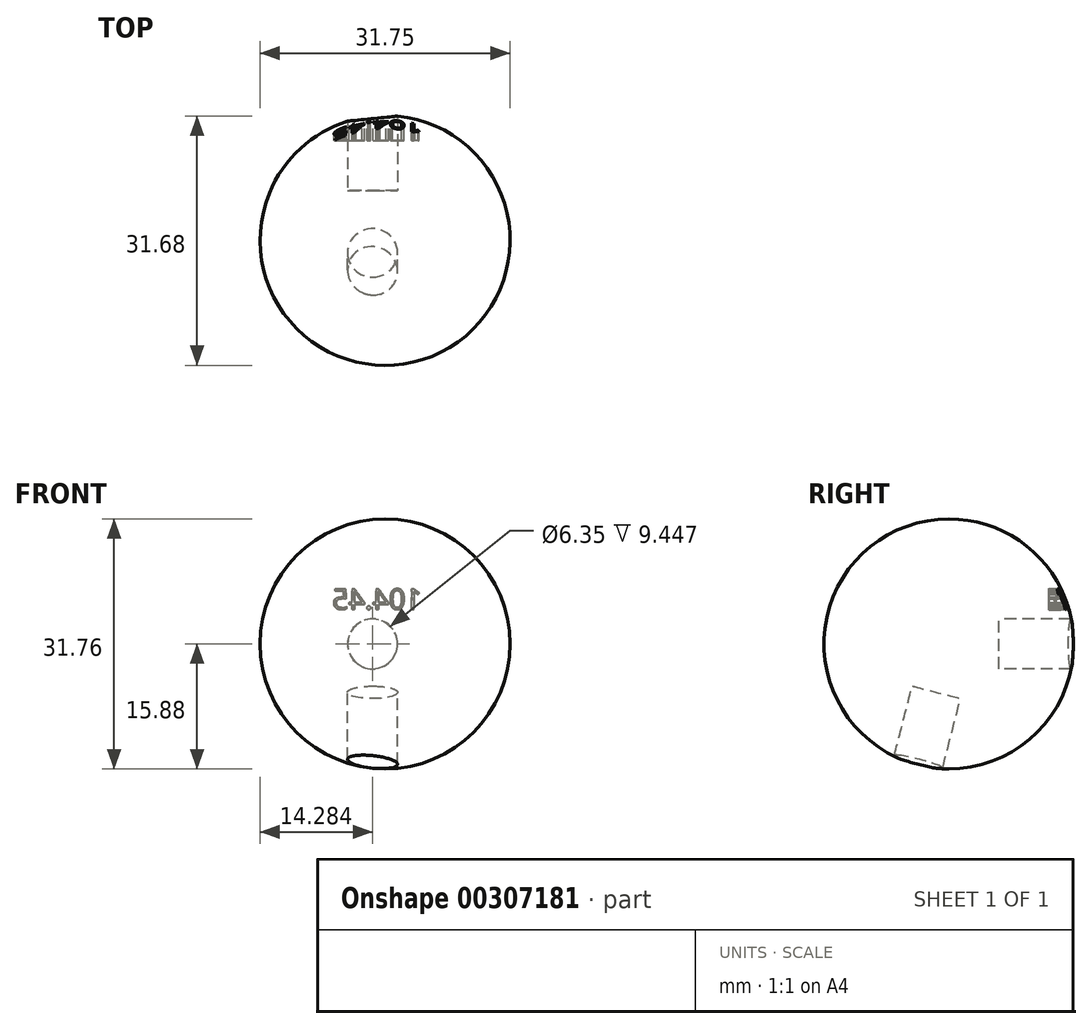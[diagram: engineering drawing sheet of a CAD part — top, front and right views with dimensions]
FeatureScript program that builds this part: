
annotation { "Feature Type Name" : "Feature", "Feature Type Description" : "" }
export const myFeature = defineFeature(function(context is Context, id is Id, definition is map)
    precondition{}
    {
        {
            var Q0;
            Q0=qCreatedBy(makeId("Top.planeOp"),FACE);
            var sketch = newSketch(context, id + "F0", { "sketchPlane" : qUnion([Q0])});
            skCircle(sketch, "E0", {"center": v(0, 0) * mm, "radius": 15.88 * mm});
            skSolve(sketch);
        }
        {
            var Q0;
            Q0=qCreatedBy(makeId("Front.planeOp"),FACE);
            var sketch = newSketch(context, id + "F1", { "sketchPlane" : qUnion([Q0])});
            skArc(sketch, "E1", {"start": v(0, 15.88) * mm, "mid": v(-15.88, 0) * mm, "end": v(0, -15.88) * mm});
            skLineSegment(sketch, "E2", {"start": v(0, -15.88) * mm, "end": v(0, 15.88) * mm});
            skSolve(sketch);
        }
        {
            var Q0;
            Q0 = qSketchRegion(id + "F1", true);
            var Q1;
            Q1=sQuery(id+"F0.wireOp",EDGE,"E0");
            revolve(context, id + "F2", {"entities" : qUnion([Q0]), "axis" : qUnion([Q1]), "revolveType" : RevolveType.FULL});
        }
        {
            var Q0;
            Q0=qCreatedBy(makeId("Front.planeOp"),FACE);
            cPlane(context, id + "F3", {"entities" : qUnion([Q0]), "cplaneType" : CPlaneType.OFFSET, "offset" : 6.35 * mm, "oppositeDirection" : true, "width" : 152.4 * mm, "height" : 152.4 * mm});
        }
        {
            var Q0;
            Q0=qCreatedBy(id+"F3.planeOp",FACE);
            var sketch = newSketch(context, id + "F4", { "sketchPlane" : qUnion([Q0])});
            skCircle(sketch, "E3", {"center": v(-1.6, 0) * mm, "radius": 3.18 * mm});
            skSolve(sketch);
        }
        {
            var Q0;
            Q0 = qSketchRegion(id + "F4", true);
            extrude(context, id + "F5", {"entities" : qUnion([Q0]), "oppositeDirection" : true, "depth" : 38.1 * mm});
        }
        {
            var Q0;
            Q0=makeQuery(id+"F5.opExtrude","CAP_FACE",FACE,{"disambiguationData":[OSD([sQuery(id+"F4.wireOp",EDGE,"E3")])],"isStart":false});
            var sketch = newSketch(context, id + "F6", { "sketchPlane" : qUnion([Q0])});
            skText(sketch, "E4", { "text": "104.45", "fontName": "OpenSans-Regular.ttf"});
            const initialGuessF6  = {"E4": [-0.00465, 0.00439, 1, 0, 0.00262]};
            skSetInitialGuess(sketch, initialGuessF6);
            skSolve(sketch);
        }
        {
            var Q0;
            Q0 = qSketchRegion(id + "F6", true);
            extrude(context, id + "F7", {"entities" : qUnion([Q0]), "operationType" : NewBodyOperationType.REMOVE, "oppositeDirection" : true, "depth" : 31.75 * mm});
        }
        {
            var Q0;
            Q0=qCreatedBy(makeId("Front.planeOp"),FACE);
            var sketch = newSketch(context, id + "F8", { "sketchPlane" : qUnion([Q0])});
            skLineSegment(sketch, "E5", {"start": v(0, 0) * mm, "end": v(0, 31.16) * mm, "construction": true});
            skLineSegment(sketch, "E6", {"start": v(0, 0) * mm, "end": v(39.64, 0) * mm, "construction": true});
            skLineSegment(sketch, "E7", {"start": v(0, 0) * mm, "end": v(-35.4, 0) * mm, "construction": true});
            skSolve(sketch);
        }
        {
            var Q0;
            Q0=makeQuery(id+"F5.opExtrude","SWEPT_BODY",BODY,{"disambiguationData":[OSD([sQuery(id+"F4.wireOp",EDGE,"E3")])]});
            var Q1;
            Q1=sQuery(id+"F8.wireOp",EDGE,"E6");
            transform(context, id + "F9", {"entities" : qUnion([Q0]), "transformType" : TransformType.ROTATION, "transformAxis" : qUnion([Q1]), "angle" : 104.45 * degree, "oppositeDirection" : true, "makeCopy" : true});
        }
        {
            var Q0;
            Q0=makeQuery(id+"F9.opPattern","COPY",BODY,{"derivedFrom":makeQuery(id+"F5.opExtrude","SWEPT_BODY",BODY,{"disambiguationData":[OSD([sQuery(id+"F4.wireOp",EDGE,"E3")])]}),"instanceName":"1"});
            var Q1;
            Q1=makeQuery(id+"F5.opExtrude","SWEPT_BODY",BODY,{"disambiguationData":[OSD([sQuery(id+"F4.wireOp",EDGE,"E3")])]});
            var Q2;
            Q2=makeQuery(id+"F2.opRevolve","SWEPT_BODY",BODY,{"disambiguationData":[OSD([sQuery(id+"F1.wireOp",EDGE,"E1"),sQuery(id+"F1.wireOp",EDGE,"E2")])]});
            booleanBodies(context, id + "F10", {"operationType" : BooleanOperationType.SUBTRACTION, "tools" : qUnion([Q0, Q1]), "targets" : qUnion([Q2])});
        }
    });
